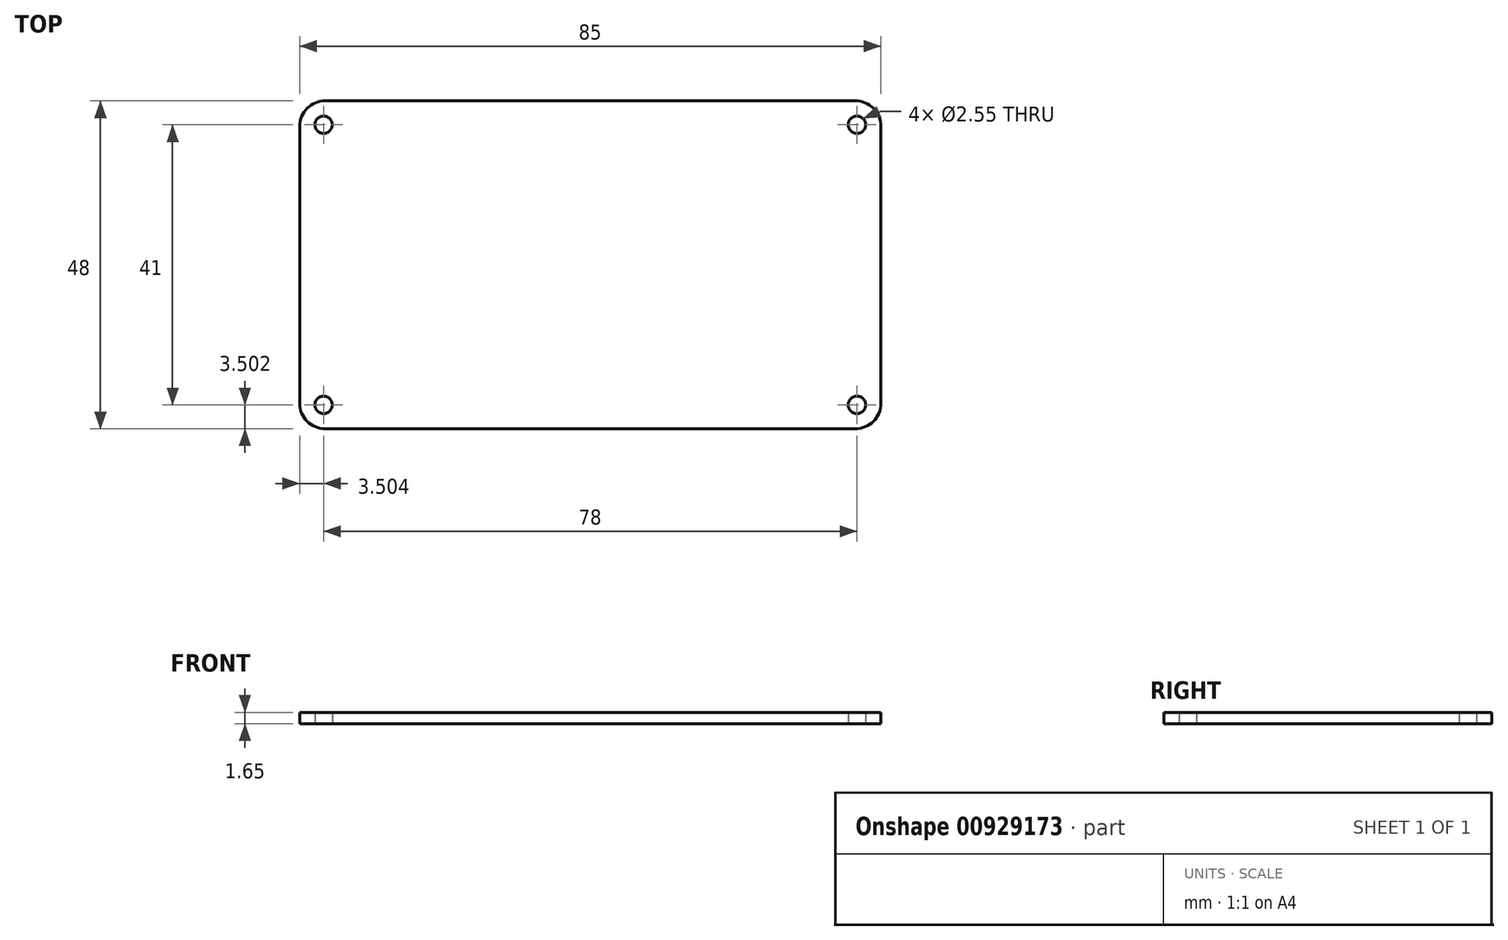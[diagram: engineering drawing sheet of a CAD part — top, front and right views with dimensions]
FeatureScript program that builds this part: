
annotation { "Feature Type Name" : "Feature", "Feature Type Description" : "" }
export const myFeature = defineFeature(function(context is Context, id is Id, definition is map)
    precondition{}
    {
        {
            var Q0;
            Q0=qCreatedBy(makeId("Top.planeOp"),FACE);
            var sketch = newSketch(context, id + "F0", { "sketchPlane" : qUnion([Q0])});
            skLineSegment(sketch, "E0.bottom", {"start": v(-32.3, -42.35) * mm, "end": v(52.7, -42.35) * mm});
            skLineSegment(sketch, "E0.top", {"start": v(-32.3, 5.65) * mm, "end": v(52.7, 5.65) * mm});
            skLineSegment(sketch, "E0.left", {"start": v(-32.3, -42.35) * mm, "end": v(-32.3, 5.65) * mm});
            skLineSegment(sketch, "E0.right", {"start": v(52.7, -42.35) * mm, "end": v(52.7, 5.65) * mm});
            skCircle(sketch, "E1", {"center": v(49.2, -38.85) * mm, "radius": 1.27 * mm});
            skCircle(sketch, "E2", {"center": v(49.2, 2.15) * mm, "radius": 1.27 * mm});
            skCircle(sketch, "E3", {"center": v(-28.8, 2.15) * mm, "radius": 1.27 * mm});
            skCircle(sketch, "E4", {"center": v(-28.8, -38.85) * mm, "radius": 1.27 * mm});
            skSolve(sketch);
        }
        {
            var Q0;
            Q0=makeQuery(id+"F0.imprint","IMPRINT",FACE,{"disambiguationData":[TD([[makeQuery(id+"F0.imprint","IMPRINT",EDGE,{"derivedFrom":sQuery(id+"F0.wireOp",EDGE,"E0.bottom")}),1.0]])]});
            extrude(context, id + "F1", {"entities" : qUnion([Q0]), "depth" : 1.65 * mm, "offsetDistance" : 25 * mm});
        }
        {
            var Q0;
            Q0=makeQuery(id+"F1.opExtrude","SWEPT_EDGE",EDGE,{"disambiguationData":[OSD([sQuery(id+"F0.wireOp",EDGE,"E0.bottom"),sQuery(id+"F0.wireOp",EDGE,"E0.right")])]});
            var Q1;
            Q1=makeQuery(id+"F1.opExtrude","SWEPT_EDGE",EDGE,{"disambiguationData":[OSD([sQuery(id+"F0.wireOp",EDGE,"E0.bottom"),sQuery(id+"F0.wireOp",EDGE,"E0.left")])]});
            var Q2;
            Q2=makeQuery(id+"F1.opExtrude","SWEPT_EDGE",EDGE,{"disambiguationData":[OSD([sQuery(id+"F0.wireOp",EDGE,"E0.top"),sQuery(id+"F0.wireOp",EDGE,"E0.left")])]});
            var Q3;
            Q3=makeQuery(id+"F1.opExtrude","SWEPT_EDGE",EDGE,{"disambiguationData":[OSD([sQuery(id+"F0.wireOp",EDGE,"E0.top"),sQuery(id+"F0.wireOp",EDGE,"E0.right")])]});
            fillet(context, id + "F2", {"entities" : qUnion([Q0, Q1, Q2, Q3]), "radius" : 3.75 * mm, "tangentPropagation" : true, "allowEdgeOverflow" : false});
        }
    });
